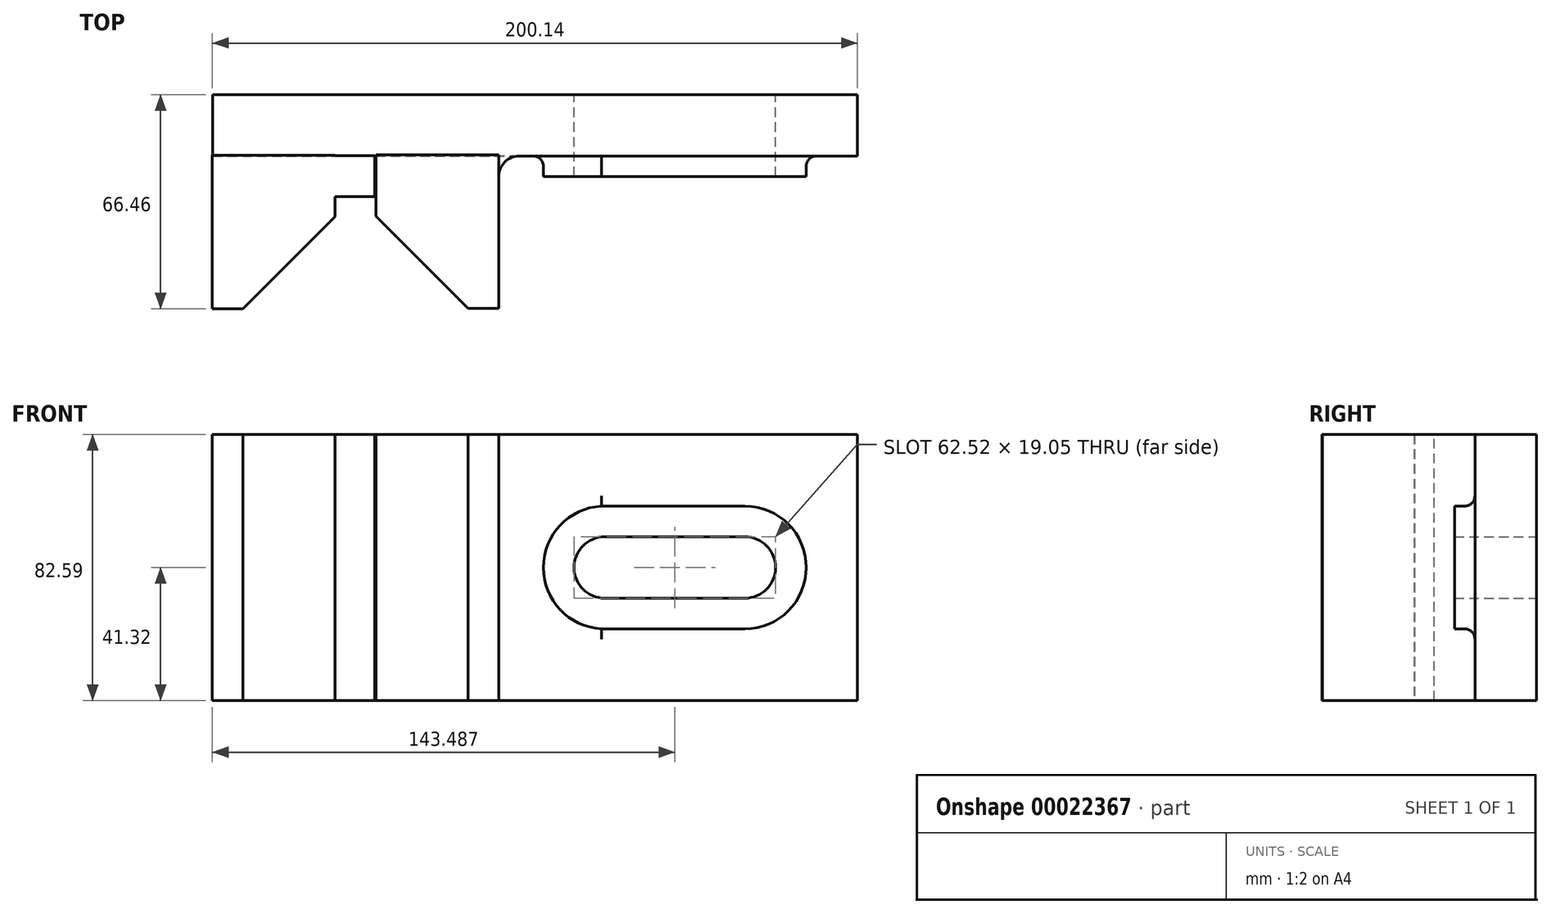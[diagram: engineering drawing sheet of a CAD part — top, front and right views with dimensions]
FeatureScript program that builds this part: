
annotation { "Feature Type Name" : "Feature", "Feature Type Description" : "" }
export const myFeature = defineFeature(function(context is Context, id is Id, definition is map)
    precondition{}
    {
        {
            var Q0;
            Q0=qCreatedBy(makeId("Front.planeOp"),FACE);
            var sketch = newSketch(context, id + "F0", { "sketchPlane" : qUnion([Q0])});
            skLineSegment(sketch, "E0.bottom", {"start": v(-117.05, 41.23) * mm, "end": v(82.97, 41.23) * mm});
            skLineSegment(sketch, "E0.top", {"start": v(-117.05, -41.32) * mm, "end": v(82.97, -41.32) * mm});
            skLineSegment(sketch, "E0.left", {"start": v(-117.05, 41.23) * mm, "end": v(-117.05, -41.32) * mm});
            skLineSegment(sketch, "E0.right", {"start": v(82.97, 41.23) * mm, "end": v(82.97, -41.32) * mm});
            skSolve(sketch);
        }
        {
            var Q0;
            Q0 = qSketchRegion(id + "F0", true);
            extrude(context, id + "F1", {"entities" : qUnion([Q0]), "depth" : 19.05 * mm});
        }
        {
            var Q0;
            Q0=qCreatedBy(makeId("Top.planeOp"),FACE);
            var sketch = newSketch(context, id + "F2", { "sketchPlane" : qUnion([Q0])});
            skLineSegment(sketch, "E1.bottom", {"start": v(-117.17, -18.84) * mm, "end": v(-79.07, -18.84) * mm});
            skLineSegment(sketch, "E1.top", {"start": v(-117.17, -66.46) * mm, "end": v(-79.07, -66.46) * mm});
            skLineSegment(sketch, "E1.left", {"start": v(-117.17, -18.84) * mm, "end": v(-117.17, -66.46) * mm});
            skLineSegment(sketch, "E1.right", {"start": v(-79.07, -18.84) * mm, "end": v(-79.07, -66.46) * mm});
            skLineSegment(sketch, "E2", {"start": v(-107.64, -66.46) * mm, "end": v(-79.07, -37.89) * mm});
            skLineSegment(sketch, "E3.MirrorCS", {"start": v(-15.57, -18.84) * mm, "end": v(-53.67, -18.84) * mm});
            skLineSegment(sketch, "E4.MirrorCS", {"start": v(-28.27, -18.84) * mm, "end": v(-66.37, -18.84) * mm});
            skSolve(sketch);
        }
        {
            var Q0;
            {var subQ2=sQuery(id+"F2.wireOp",EDGE,"E1.bottom");Q0=makeQuery(id+"F2.imprint","IMPRINT",FACE,{"disambiguationData":[TD([[makeQuery(id+"F2.imprint","IMPRINT",EDGE,{"derivedFrom":subQ2}),-1.0]])]});}
            extrude(context, id + "F3", {"entities" : qUnion([Q0]), "endBound" : BoundingType.SYMMETRIC, "depth" : 82.55 * mm});
        }
        {
            var Q0;
            Q0=qCreatedBy(makeId("Top.planeOp"),FACE);
            var sketch = newSketch(context, id + "F4", { "sketchPlane" : qUnion([Q0])});
            skLineSegment(sketch, "E5.bottom", {"start": v(-79.45, -31.69) * mm, "end": v(-66.75, -31.69) * mm});
            skLineSegment(sketch, "E5.top", {"start": v(-79.45, -18.99) * mm, "end": v(-66.75, -18.99) * mm});
            skLineSegment(sketch, "E5.left", {"start": v(-79.45, -31.69) * mm, "end": v(-79.45, -18.99) * mm});
            skLineSegment(sketch, "E5.right", {"start": v(-66.75, -31.69) * mm, "end": v(-66.75, -18.99) * mm});
            skSolve(sketch);
        }
        {
            var Q0;
            Q0 = qSketchRegion(id + "F4", true);
            extrude(context, id + "F5", {"entities" : qUnion([Q0]), "operationType" : NewBodyOperationType.ADD, "endBound" : BoundingType.SYMMETRIC, "depth" : 82.55 * mm});
        }
        {
            var Q0;
            Q0=qCreatedBy(makeId("Top.planeOp"),FACE);
            var sketch = newSketch(context, id + "F6", { "sketchPlane" : qUnion([Q0])});
            skLineSegment(sketch, "E6.bottom", {"start": v(-66.37, -18.76) * mm, "end": v(-28.27, -18.76) * mm});
            skLineSegment(sketch, "E6.top", {"start": v(-66.37, -66.38) * mm, "end": v(-28.27, -66.38) * mm});
            skLineSegment(sketch, "E6.left", {"start": v(-66.37, -18.76) * mm, "end": v(-66.37, -66.38) * mm});
            skLineSegment(sketch, "E6.right", {"start": v(-28.27, -18.76) * mm, "end": v(-28.27, -66.38) * mm});
            skLineSegment(sketch, "E7", {"start": v(-66.37, -37.8) * mm, "end": v(-37.8, -66.38) * mm});
            skSolve(sketch);
        }
        {
            var Q0;
            {var subQ3=sQuery(id+"F6.wireOp",EDGE,"E6.bottom");Q0=makeQuery(id+"F6.imprint","IMPRINT",FACE,{"disambiguationData":[TD([[makeQuery(id+"F6.imprint","IMPRINT",EDGE,{"derivedFrom":subQ3}),-1.0]])]});}
            extrude(context, id + "F7", {"entities" : qUnion([Q0]), "operationType" : NewBodyOperationType.ADD, "endBound" : BoundingType.SYMMETRIC, "depth" : 82.55 * mm});
        }
        {
            var Q0;
            Q0=makeQuery(id+"F7.boolean.opBoolean","INTERSECT",EDGE,{"derivedFrom":[makeQuery(id+"F1.opExtrude","CAP_FACE",FACE,{"disambiguationData":[OSD([sQuery(id+"F0.wireOp",EDGE,"E0.bottom"),sQuery(id+"F0.wireOp",EDGE,"E0.top"),sQuery(id+"F0.wireOp",EDGE,"E0.left"),sQuery(id+"F0.wireOp",EDGE,"E0.right")])],"isStart":false}),makeQuery(id+"F7.opExtrude","SWEPT_FACE",FACE,{"disambiguationData":[OSD([sQuery(id+"F6.wireOp",EDGE,"E6.right")])]})]});
            fillet(context, id + "F8", {"entities" : qUnion([Q0]), "radius" : 6.35 * mm, "tangentPropagation" : true, "allowEdgeOverflow" : false});
        }
        {
            var Q0;
            Q0=makeQuery(id+"F1.opExtrude","CAP_FACE",FACE,{"disambiguationData":[OSD([sQuery(id+"F0.wireOp",EDGE,"E0.bottom"),sQuery(id+"F0.wireOp",EDGE,"E0.top"),sQuery(id+"F0.wireOp",EDGE,"E0.left"),sQuery(id+"F0.wireOp",EDGE,"E0.right")])],"isStart":false});
            var sketch = newSketch(context, id + "F9", { "sketchPlane" : qUnion([Q0])});
            skCircle(sketch, "E8", {"center": v(48.05, 0) * mm, "radius": 19.05 * mm});
            skCircle(sketch, "E9", {"center": v(48.05, 0) * mm, "radius": 9.53 * mm});
            skLineSegment(sketch, "E10", {"start": v(48.05, 0) * mm, "end": v(48.05, -19.05) * mm});
            skLineSegment(sketch, "E11", {"start": v(48.05, -19.05) * mm, "end": v(48.05, 19.05) * mm});
            skLineSegment(sketch, "E12.left", {"start": v(48.05, -19.05) * mm, "end": v(48.05, -9.52) * mm});
            skLineSegment(sketch, "E13.left", {"start": v(48.05, 19.05) * mm, "end": v(48.05, 9.53) * mm});
            skLineSegment(sketch, "E14.bottom", {"start": v(48.05, -19.05) * mm, "end": v(3.6, -19.05) * mm});
            skLineSegment(sketch, "E14.top", {"start": v(48.05, -9.52) * mm, "end": v(3.6, -9.53) * mm});
            skLineSegment(sketch, "E14.right", {"start": v(3.6, -19.05) * mm, "end": v(3.6, -9.53) * mm});
            skLineSegment(sketch, "E15.bottom", {"start": v(48.05, 9.53) * mm, "end": v(3.6, 9.53) * mm});
            skLineSegment(sketch, "E15.top", {"start": v(48.05, 19.05) * mm, "end": v(3.6, 19.05) * mm});
            skLineSegment(sketch, "E15.left", {"start": v(48.05, 9.53) * mm, "end": v(48.05, 19.05) * mm});
            skLineSegment(sketch, "E15.right", {"start": v(3.6, 9.53) * mm, "end": v(3.6, 19.05) * mm});
            skCircle(sketch, "E16", {"center": v(4.58, 0) * mm, "radius": 9.53 * mm});
            skCircle(sketch, "E17", {"center": v(4.58, 0) * mm, "radius": 19.05 * mm});
            skSolve(sketch);
        }
        {
            var Q0;
            Q0 = qSketchRegion(id + "F9", true);
            var Q1;
            {var subQ0=sQuery(id+"F9.wireOp",EDGE,"E12.left");Q1=makeQuery(id+"F9.imprint","IMPRINT",FACE,{"disambiguationData":[TD([[makeQuery(id+"F9.imprint","IMPRINT",EDGE,{"derivedFrom":subQ0}),1.0]])]});}
            var Q2;
            {var subQ0=sQuery(id+"F9.wireOp",EDGE,"E15.left");Q2=makeQuery(id+"F9.imprint","IMPRINT",FACE,{"disambiguationData":[TD([[makeQuery(id+"F9.imprint","IMPRINT",EDGE,{"derivedFrom":subQ0}),1.0]])]});}
            extrude(context, id + "F10", {"entities" : qUnion([Q0, Q1, Q2]), "operationType" : NewBodyOperationType.ADD, "depth" : 6.35 * mm});
        }
        {
            var Q0;
            Q0=makeQuery(id+"F10.opExtrude","CAP_EDGE",EDGE,{"disambiguationData":[OSD([sQuery(id+"F9.wireOp",EDGE,"E15.top")])],"isStart":true});
            fillet(context, id + "F11", {"entities" : qUnion([Q0]), "radius" : 3.17 * mm, "tangentPropagation" : true, "allowEdgeOverflow" : false});
        }
        {
            var Q0;
            Q0=makeQuery(id+"F10.opExtrude","CAP_EDGE",EDGE,{"disambiguationData":[OSD([sQuery(id+"F9.wireOp",EDGE,"E17")])],"isStart":true});
            fillet(context, id + "F12", {"entities" : qUnion([Q0]), "radius" : 3.17 * mm, "tangentPropagation" : true, "allowEdgeOverflow" : false});
        }
        {
            var Q0;
            Q0=makeQuery(id+"F10.boolean.opBoolean","SPLIT",FACE,{"disambiguationData":[TD([makeQuery(id+"F10.opExtrude","SWEPT_FACE",FACE,{"disambiguationData":[OSD([sQuery(id+"F9.wireOp",EDGE,"E9")])]})])],"derivedFrom":makeQuery(id+"F1.opExtrude","CAP_FACE",FACE,{"disambiguationData":[OSD([sQuery(id+"F0.wireOp",EDGE,"E0.bottom"),sQuery(id+"F0.wireOp",EDGE,"E0.top"),sQuery(id+"F0.wireOp",EDGE,"E0.left"),sQuery(id+"F0.wireOp",EDGE,"E0.right")])],"isStart":false})});
            extrude(context, id + "F13", {"entities" : qUnion([Q0]), "operationType" : NewBodyOperationType.REMOVE, "oppositeDirection" : true, "depth" : 25.4 * mm});
        }
    });
